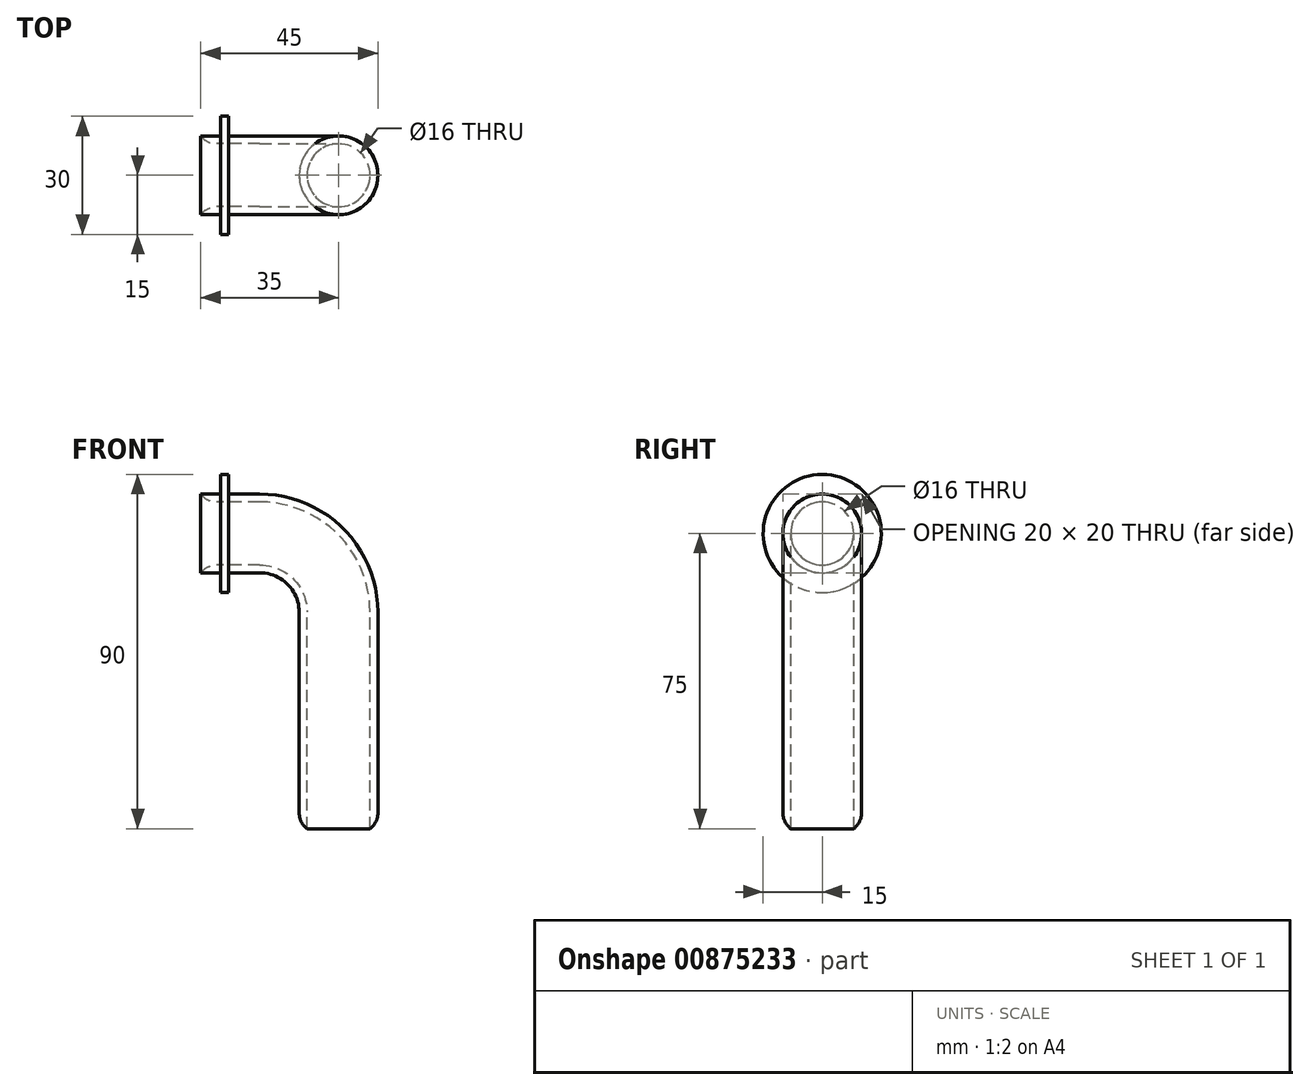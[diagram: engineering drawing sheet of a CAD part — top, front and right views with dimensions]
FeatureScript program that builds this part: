
annotation { "Feature Type Name" : "Feature", "Feature Type Description" : "" }
export const myFeature = defineFeature(function(context is Context, id is Id, definition is map)
    precondition{}
    {
        {
            var Q0;
            Q0=qCreatedBy(makeId("Front.planeOp"),FACE);
            var sketch = newSketch(context, id + "F0", { "sketchPlane" : qUnion([Q0])});
            skLineSegment(sketch, "E0", {"start": v(-35, 30) * mm, "end": v(-20, 30) * mm});
            skLineSegment(sketch, "E1", {"start": v(0, 10) * mm, "end": v(0, -45) * mm});
            skPoint(sketch, "E2.visualSharp", {"position": v(0, 30) * mm});
            skArc(sketch, "E2.filletArc", {"start": v(0, 10) * mm, "mid": v(-5.86, 24.14) * mm, "end": v(-20, 30) * mm});
            skSolve(sketch);
        }
        {
            var Q0;
            Q0=sQuery(id+"F0.wireOp",VERTEX,"E1.end");
            var Q1;
            Q1=qCreatedBy(makeId("Top.planeOp"),FACE);
            cPlane(context, id + "F1", {"entities" : qUnion([Q0, Q1]), "cplaneType" : CPlaneType.PLANE_POINT, "offset" : 25 * mm, "width" : 150 * mm, "height" : 150 * mm});
        }
        {
            var Q0;
            Q0=qCreatedBy(id+"F1.planeOp",FACE);
            var sketch = newSketch(context, id + "F2", { "sketchPlane" : qUnion([Q0])});
            skCircle(sketch, "E3", {"center": v(0, 0) * mm, "radius": 10 * mm});
            skCircle(sketch, "E4", {"center": v(0, 0) * mm, "radius": 8 * mm});
            skSolve(sketch);
        }
        {
            var Q0;
            Q0=makeQuery(id+"F2.imprint","IMPRINT",FACE,{"disambiguationData":[TD([[makeQuery(id+"F2.imprint","IMPRINT",EDGE,{"derivedFrom":sQuery(id+"F2.wireOp",EDGE,"E3")}),1.0]])]});
            var Q1;
            Q1=sQuery(id+"F0.wireOp",EDGE,"E1");
            var Q2;
            Q2=sQuery(id+"F0.wireOp",EDGE,"E2.filletArc");
            var Q3;
            Q3=sQuery(id+"F0.wireOp",EDGE,"E0");
            sweep(context, id + "F3", {"profiles" : qUnion([Q0]), "path" : qUnion([Q1, Q2, Q3])});
        }
        {
            var Q0;
            Q0=makeQuery(id+"F3.opSweep","CAP_EDGE",EDGE,{"disambiguationData":[OSD([sQuery(id+"F0.wireOp",VERTEX,"E1.end"),sQuery(id+"F2.wireOp",EDGE,"E3")])],"isStart":true});
            fillet(context, id + "F4", {"entities" : qUnion([Q0]), "radius" : 5 * mm, "tangentPropagation" : true, "allowEdgeOverflow" : false});
        }
        {
            var Q0;
            Q0=makeQuery(id+"F3.opSweep","CAP_EDGE",EDGE,{"disambiguationData":[OSD([sQuery(id+"F0.wireOp",VERTEX,"E0.start"),sQuery(id+"F2.wireOp",EDGE,"E4")])],"isStart":false});
            fillet(context, id + "F5", {"entities" : qUnion([Q0]), "radius" : 5 * mm, "tangentPropagation" : true, "allowEdgeOverflow" : false});
        }
        {
            var Q0;
            Q0=qCreatedBy(makeId("Right.planeOp"),FACE);
            cPlane(context, id + "F6", {"entities" : qUnion([Q0]), "cplaneType" : CPlaneType.OFFSET, "offset" : 30 * mm, "oppositeDirection" : true, "width" : 150 * mm, "height" : 150 * mm});
        }
        {
            var Q0;
            Q0=qCreatedBy(id+"F6.planeOp",FACE);
            var sketch = newSketch(context, id + "F7", { "sketchPlane" : qUnion([Q0])});
            skCircle(sketch, "E5", {"center": v(0, 30) * mm, "radius": 10 * mm});
            skCircle(sketch, "E6", {"center": v(0, 30) * mm, "radius": 15 * mm});
            skSolve(sketch);
        }
        {
            var Q0;
            Q0=makeQuery(id+"F7.imprint","IMPRINT",FACE,{"disambiguationData":[TD([[makeQuery(id+"F7.imprint","IMPRINT",EDGE,{"derivedFrom":sQuery(id+"F7.wireOp",EDGE,"E5")}),-1.0]])]});
            extrude(context, id + "F8", {"entities" : qUnion([Q0]), "operationType" : NewBodyOperationType.ADD, "depth" : 2 * mm, "offsetDistance" : 25 * mm});
        }
    });
